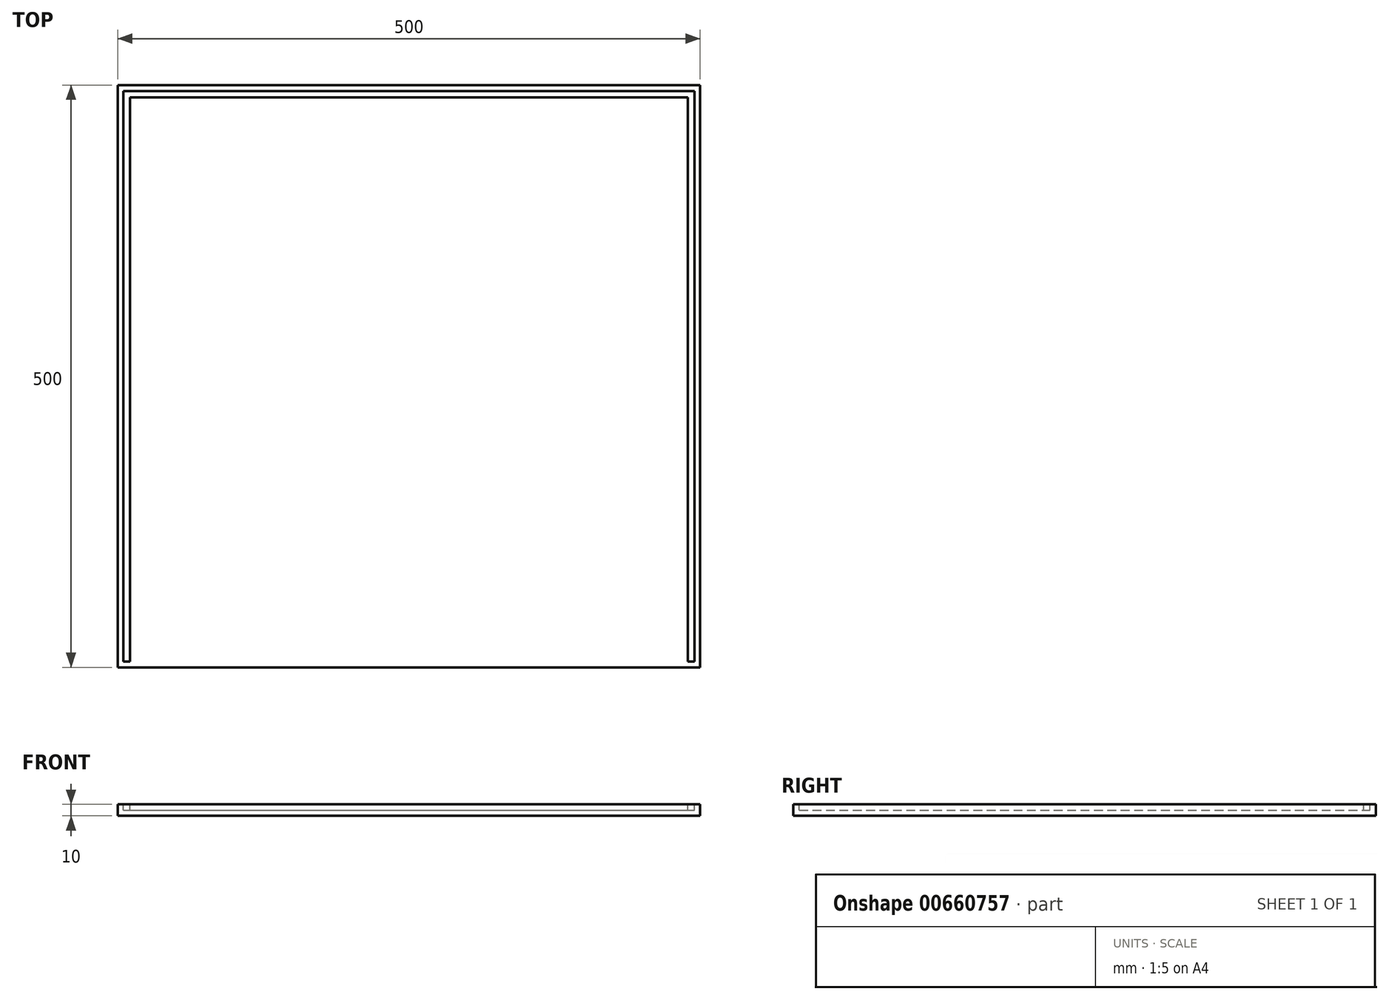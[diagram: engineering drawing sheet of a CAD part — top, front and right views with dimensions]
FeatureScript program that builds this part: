
annotation { "Feature Type Name" : "Feature", "Feature Type Description" : "" }
export const myFeature = defineFeature(function(context is Context, id is Id, definition is map)
    precondition{}
    {
        {
            var Q0;
            Q0=qCreatedBy(makeId("Top.planeOp"),FACE);
            var sketch = newSketch(context, id + "F0", { "sketchPlane" : qUnion([Q0])});
            skLineSegment(sketch, "E0.bottom", {"start": v(0, 0) * mm, "end": v(500, 0) * mm});
            skLineSegment(sketch, "E0.top", {"start": v(0, 500) * mm, "end": v(500, 500) * mm});
            skLineSegment(sketch, "E0.left", {"start": v(0, 0) * mm, "end": v(0, 500) * mm});
            skLineSegment(sketch, "E0.right", {"start": v(500, 0) * mm, "end": v(500, 500) * mm});
            skSolve(sketch);
        }
        {
            var Q0;
            Q0=qSketchRegion(id+"F0",true);
            extrude(context, id + "F1", {"entities" : qUnion([Q0]), "depth" : 10 * mm, "offsetDistance" : 25 * mm});
        }
        {
            var Q0;
            Q0=makeQuery(id+"F1.opExtrude","CAP_FACE",FACE,{"disambiguationData":[OSD([sQuery(id+"F0.wireOp",EDGE,"E0.bottom"),sQuery(id+"F0.wireOp",EDGE,"E0.top"),sQuery(id+"F0.wireOp",EDGE,"E0.left"),sQuery(id+"F0.wireOp",EDGE,"E0.right")])],"isStart":false});
            var sketch = newSketch(context, id + "F2", { "sketchPlane" : qUnion([Q0])});
            skLineSegment(sketch, "E1.bottom", {"start": v(5, 5) * mm, "end": v(10.5, 5) * mm});
            skLineSegment(sketch, "E1.top", {"start": v(5, 495) * mm, "end": v(10.5, 495) * mm});
            skLineSegment(sketch, "E1.left", {"start": v(5, 5) * mm, "end": v(5, 495) * mm});
            skLineSegment(sketch, "E1.right", {"start": v(10.5, 5) * mm, "end": v(10.5, 495) * mm});
            skLineSegment(sketch, "E2.bottom", {"start": v(10.5, 495) * mm, "end": v(489.5, 495) * mm});
            skLineSegment(sketch, "E2.top", {"start": v(10.5, 489.5) * mm, "end": v(489.5, 489.5) * mm});
            skLineSegment(sketch, "E2.left", {"start": v(10.5, 495) * mm, "end": v(10.5, 489.5) * mm});
            skLineSegment(sketch, "E2.right", {"start": v(489.5, 495) * mm, "end": v(489.5, 489.5) * mm});
            skLineSegment(sketch, "E3.bottom", {"start": v(489.5, 495) * mm, "end": v(495, 495) * mm});
            skLineSegment(sketch, "E3.top", {"start": v(489.5, 5) * mm, "end": v(495, 5) * mm});
            skLineSegment(sketch, "E3.left", {"start": v(489.5, 495) * mm, "end": v(489.5, 5) * mm});
            skLineSegment(sketch, "E3.right", {"start": v(495, 495) * mm, "end": v(495, 5) * mm});
            skSolve(sketch);
        }
        {
            var Q0;
            {var subQ0=sQuery(id+"F2.wireOp",EDGE,"E2.bottom");Q0=makeQuery(id+"F2.imprint","IMPRINT",FACE,{"disambiguationData":[TD([[makeQuery(id+"F2.imprint","IMPRINT",EDGE,{"derivedFrom":subQ0}),-1.0]])]});}
            var Q1;
            Q1=makeQuery(id+"F2.imprint","IMPRINT",FACE,{"disambiguationData":[TD([[makeQuery(id+"F2.imprint","IMPRINT",EDGE,{"derivedFrom":sQuery(id+"F2.wireOp",EDGE,"E1.bottom")}),1.0]])]});
            var Q2;
            {var subQ3=sQuery(id+"F2.wireOp",EDGE,"E3.bottom");Q2=makeQuery(id+"F2.imprint","IMPRINT",FACE,{"disambiguationData":[TD([[makeQuery(id+"F2.imprint","IMPRINT",EDGE,{"derivedFrom":subQ3}),-1.0]])]});}
            extrude(context, id + "F3", {"entities" : qUnion([Q0, Q1, Q2]), "operationType" : NewBodyOperationType.REMOVE, "oppositeDirection" : true, "depth" : 5 * mm, "offsetDistance" : 25 * mm});
        }
    });
